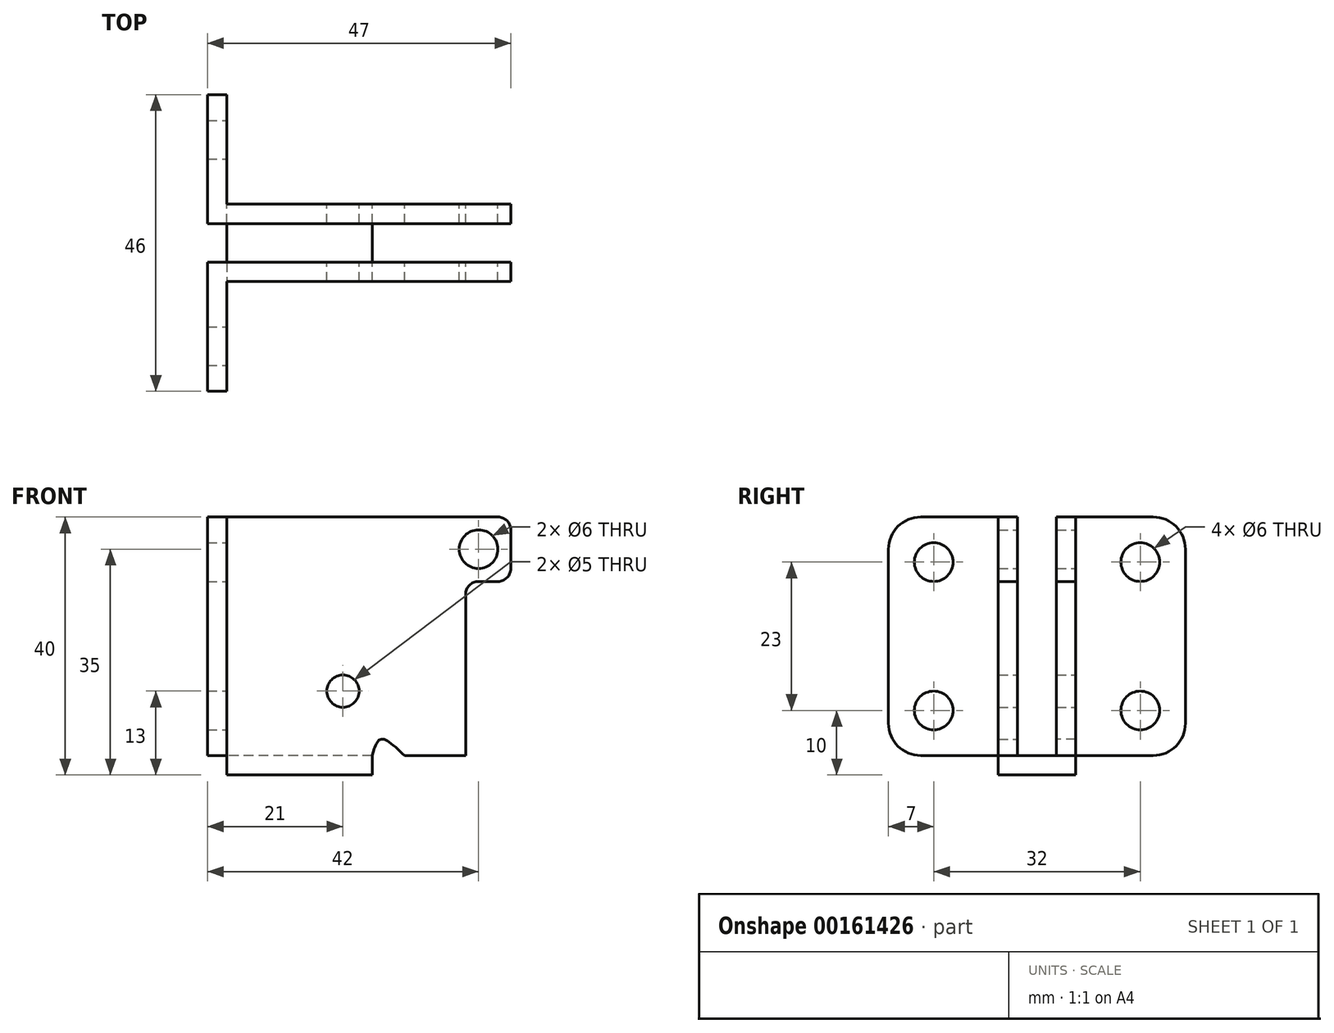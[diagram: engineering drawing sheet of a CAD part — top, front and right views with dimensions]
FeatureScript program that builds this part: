
annotation { "Feature Type Name" : "Feature", "Feature Type Description" : "" }
export const myFeature = defineFeature(function(context is Context, id is Id, definition is map)
    precondition{}
    {
        {
            var Q0;
            Q0=qCreatedBy(makeId("Right.planeOp"),FACE);
            var sketch = newSketch(context, id + "F0", { "sketchPlane" : qUnion([Q0])});
            skLineSegment(sketch, "E0.bottom", {"start": v(6, 20) * mm, "end": v(3, 20) * mm});
            skLineSegment(sketch, "E0.top", {"start": v(6, -20) * mm, "end": v(-6, -20) * mm});
            skLineSegment(sketch, "E0.left", {"start": v(6, 20) * mm, "end": v(6, -20) * mm});
            skLineSegment(sketch, "E0.right", {"start": v(-6, 20) * mm, "end": v(-6, -20) * mm});
            skPoint(sketch, "E0.middle", {"position": v(0, 0) * mm});
            skLineSegment(sketch, "E1", {"start": v(-3, 20) * mm, "end": v(-3, -17) * mm});
            skLineSegment(sketch, "E2", {"start": v(-3, -17) * mm, "end": v(3, -17) * mm});
            skLineSegment(sketch, "E3", {"start": v(3, -17) * mm, "end": v(3, 20) * mm});
            skLineSegment(sketch, "E4.trimOffspring", {"start": v(-3, 20) * mm, "end": v(-6, 20) * mm});
            skSolve(sketch);
        }
        {
            var Q0;
            Q0 = qSketchRegion(id + "F0", true);
            extrude(context, id + "F1", {"entities" : qUnion([Q0]), "depth" : 44 * mm});
        }
        {
            var Q0;
            Q0=makeQuery(id+"F1.opExtrude","CAP_FACE",FACE,{"disambiguationData":[OSD([sQuery(id+"F0.wireOp",EDGE,"E0.bottom"),sQuery(id+"F0.wireOp",EDGE,"E0.top"),sQuery(id+"F0.wireOp",EDGE,"E0.left"),sQuery(id+"F0.wireOp",EDGE,"E0.right"),sQuery(id+"F0.wireOp",EDGE,"E1"),sQuery(id+"F0.wireOp",EDGE,"E2"),sQuery(id+"F0.wireOp",EDGE,"E3"),sQuery(id+"F0.wireOp",EDGE,"E4.trimOffspring")])],"isStart":true});
            var sketch = newSketch(context, id + "F2", { "sketchPlane" : qUnion([Q0])});
            skLineSegment(sketch, "E5.bottom", {"start": v(-3, 20) * mm, "end": v(-18, 20) * mm});
            skLineSegment(sketch, "E5.top", {"start": v(-3, -17) * mm, "end": v(-18, -17) * mm});
            skLineSegment(sketch, "E5.left", {"start": v(-3, 20) * mm, "end": v(-3, -17) * mm});
            skLineSegment(sketch, "E5.right", {"start": v(-23, 15) * mm, "end": v(-23, -12) * mm});
            skLineSegment(sketch, "E6.bottom", {"start": v(3, 20) * mm, "end": v(18, 20) * mm});
            skLineSegment(sketch, "E6.top", {"start": v(3, -17) * mm, "end": v(18, -17) * mm});
            skLineSegment(sketch, "E6.left", {"start": v(3, 20) * mm, "end": v(3, -17) * mm});
            skLineSegment(sketch, "E6.right", {"start": v(23, 15) * mm, "end": v(23, -12) * mm});
            skCircle(sketch, "E7", {"center": v(-16, 13) * mm, "radius": 3 * mm});
            skCircle(sketch, "E8", {"center": v(-16, -10) * mm, "radius": 3 * mm});
            skCircle(sketch, "E9", {"center": v(16, -10) * mm, "radius": 3 * mm});
            skCircle(sketch, "E10", {"center": v(16, 13) * mm, "radius": 3 * mm});
            skPoint(sketch, "E11.visualSharp", {"position": v(-23, 20) * mm});
            skArc(sketch, "E11.filletArc", {"start": v(-18, 20) * mm, "mid": v(-21.54, 18.54) * mm, "end": v(-23, 15) * mm});
            skPoint(sketch, "E12.visualSharp", {"position": v(-23, -17) * mm});
            skArc(sketch, "E12.filletArc", {"start": v(-23, -12) * mm, "mid": v(-21.54, -15.54) * mm, "end": v(-18, -17) * mm});
            skPoint(sketch, "E13.visualSharp", {"position": v(23, -17) * mm});
            skArc(sketch, "E13.filletArc", {"start": v(18, -17) * mm, "mid": v(21.54, -15.54) * mm, "end": v(23, -12) * mm});
            skPoint(sketch, "E14.visualSharp", {"position": v(23, 20) * mm});
            skArc(sketch, "E14.filletArc", {"start": v(23, 15) * mm, "mid": v(21.54, 18.54) * mm, "end": v(18, 20) * mm});
            skSolve(sketch);
        }
        {
            var Q0;
            Q0 = qSketchRegion(id + "F2", true);
            extrude(context, id + "F3", {"entities" : qUnion([Q0]), "operationType" : NewBodyOperationType.ADD, "depth" : 3 * mm});
        }
        {
            var Q0;
            Q0=makeQuery(id+"F1.opExtrude","SWEPT_FACE",FACE,{"disambiguationData":[OSD([sQuery(id+"F0.wireOp",EDGE,"E0.top")])]});
            var sketch = newSketch(context, id + "F4", { "sketchPlane" : qUnion([Q0])});
            skLineSegment(sketch, "E15.bottom", {"start": v(44, 6) * mm, "end": v(22.53, 6) * mm});
            skLineSegment(sketch, "E15.top", {"start": v(44, -6) * mm, "end": v(22.53, -6) * mm});
            skLineSegment(sketch, "E15.left", {"start": v(44, 6) * mm, "end": v(44, -6) * mm});
            skLineSegment(sketch, "E15.right", {"start": v(22.53, 6) * mm, "end": v(22.53, -6) * mm});
            skLineSegment(sketch, "E16", {"start": v(2.53, 6) * mm, "end": v(2.53, -6) * mm});
            skSolve(sketch);
        }
        {
            var Q0;
            Q0=makeQuery(id+"F4.imprint","IMPRINT",FACE,{"disambiguationData":[TD([[makeQuery(id+"F4.imprint","IMPRINT",EDGE,{"derivedFrom":sQuery(id+"F4.wireOp",EDGE,"E15.bottom")}),1.0]])]});
            extrude(context, id + "F5", {"entities" : qUnion([Q0]), "operationType" : NewBodyOperationType.REMOVE, "oppositeDirection" : true, "depth" : 3 * mm});
        }
        {
            var Q0;
            Q0=makeQuery(id+"F1.opExtrude","SWEPT_FACE",FACE,{"disambiguationData":[OSD([sQuery(id+"F0.wireOp",EDGE,"E0.left")])]});
            var sketch = newSketch(context, id + "F6", { "sketchPlane" : qUnion([Q0])});
            skLineSegment(sketch, "E17", {"start": v(-27.53, -17) * mm, "end": v(-22.53, -17) * mm});
            skPoint(sketch, "E18.0.internal.orphan", {"position": v(-22.53, -17) * mm});
            skPoint(sketch, "E18.endDerivative.orphan", {"position": v(-27.53, -17) * mm});
            skFitSpline(sketch, "E19", {"points": [v(-22.53, -17) * mm, v(-23.4, -14.8) * mm, v(-24.31, -14.47) * mm, v(-27.53, -17) * mm], "startDerivative": vector(-2.22, 7.7) * mm, "endDerivative": vector(-8.18, -7.86) * mm});
            skLineSegment(sketch, "E20.bottom", {"start": v(-44, -17) * mm, "end": v(-37, -17) * mm});
            skLineSegment(sketch, "E20.top", {"start": v(-42, 10) * mm, "end": v(-39, 10) * mm});
            skLineSegment(sketch, "E20.right", {"start": v(-37, -17) * mm, "end": v(-37, 8) * mm});
            skCircle(sketch, "E21", {"center": v(-39, 15) * mm, "radius": 3 * mm});
            skLineSegment(sketch, "E22.bottom", {"start": v(-44, 10) * mm, "end": v(-44, 10) * mm});
            skLineSegment(sketch, "E22.top", {"start": v(-44, 20) * mm, "end": v(-44, 20) * mm});
            skLineSegment(sketch, "E22.left", {"start": v(-44, 12) * mm, "end": v(-44, 18) * mm});
            skLineSegment(sketch, "E22.right", {"start": v(-44, 12) * mm, "end": v(-44, 18) * mm});
            skLineSegment(sketch, "E23", {"start": v(0, 20) * mm, "end": v(-42, 20) * mm});
            skPoint(sketch, "E24.visualSharp", {"position": v(-44, 10) * mm});
            skArc(sketch, "E24.filletArc", {"start": v(-44, 12) * mm, "mid": v(-43.41, 10.59) * mm, "end": v(-42, 10) * mm});
            skPoint(sketch, "E25.visualSharp", {"position": v(-44, 20) * mm});
            skArc(sketch, "E25.filletArc", {"start": v(-42, 20) * mm, "mid": v(-43.41, 19.41) * mm, "end": v(-44, 18) * mm});
            skPoint(sketch, "E26.visualSharp", {"position": v(-37, 10) * mm});
            skArc(sketch, "E26.filletArc", {"start": v(-37, 8) * mm, "mid": v(-37.59, 9.41) * mm, "end": v(-39, 10) * mm});
            skLineSegment(sketch, "E27", {"start": v(-22.53, -17) * mm, "end": v(-22.53, -20) * mm});
            skLineSegment(sketch, "E28", {"start": v(-22.53, -20) * mm, "end": v(0, -20) * mm});
            skLineSegment(sketch, "E29", {"start": v(0, -20) * mm, "end": v(0, 20) * mm});
            skLineSegment(sketch, "E30.top", {"start": v(0, -20) * mm, "end": v(-2, -20) * mm});
            skLineSegment(sketch, "E30.left", {"start": v(0, -17) * mm, "end": v(0, -20) * mm});
            skLineSegment(sketch, "E30.right", {"start": v(-2, -19) * mm, "end": v(-2, -20) * mm});
            skPoint(sketch, "E31.visualSharp", {"position": v(-2, -16) * mm});
            skArc(sketch, "E31.filletArc", {"start": v(0, -17) * mm, "mid": v(-1.41, -17.59) * mm, "end": v(-2, -19) * mm});
            skCircle(sketch, "E32", {"center": v(-18, -7) * mm, "radius": 2.5 * mm});
            skSolve(sketch);
        }
        {
            var Q0;
            {var subQ1=sQuery(id+"F6.wireOp",EDGE,"E20.bottom");Q0=makeQuery(id+"F6.imprint","IMPRINT",FACE,{"disambiguationData":[TD([[makeQuery(id+"F6.imprint","IMPRINT",EDGE,{"derivedFrom":subQ1}),1.0]])]});}
            var Q1;
            Q1=makeQuery(id+"F6.imprint","IMPRINT",FACE,{"disambiguationData":[TD([[makeQuery(id+"F6.imprint","IMPRINT",EDGE,{"derivedFrom":sQuery(id+"F6.wireOp",EDGE,"E21")}),1.0]])]});
            var Q2;
            {var subQ0=sQuery(id+"F6.wireOp",EDGE,"E25.filletArc");Q2=makeQuery(id+"F6.imprint","IMPRINT",FACE,{"disambiguationData":[TD([[makeQuery(id+"F6.imprint","IMPRINT",EDGE,{"derivedFrom":subQ0}),-1.0]])]});}
            var Q3;
            Q3=makeQuery(id+"F6.imprint","IMPRINT",FACE,{"disambiguationData":[TD([[makeQuery(id+"F6.imprint","IMPRINT",EDGE,{"derivedFrom":sQuery(id+"F6.wireOp",EDGE,"E30.top")}),1.0]])]});
            var Q4;
            Q4=makeQuery(id+"F6.imprint","IMPRINT",FACE,{"disambiguationData":[TD([[makeQuery(id+"F6.imprint","IMPRINT",EDGE,{"derivedFrom":sQuery(id+"F6.wireOp",EDGE,"E17")}),1.0]])]});
            var Q5;
            Q5=makeQuery(id+"F6.imprint","IMPRINT",FACE,{"disambiguationData":[TD([[makeQuery(id+"F6.imprint","IMPRINT",EDGE,{"derivedFrom":sQuery(id+"F6.wireOp",EDGE,"E32")}),1.0]])]});
            extrude(context, id + "F7", {"entities" : qUnion([Q0, Q1, Q2, Q3, Q4, Q5]), "operationType" : NewBodyOperationType.REMOVE, "oppositeDirection" : true, "depth" : 25 * mm});
        }
    });
